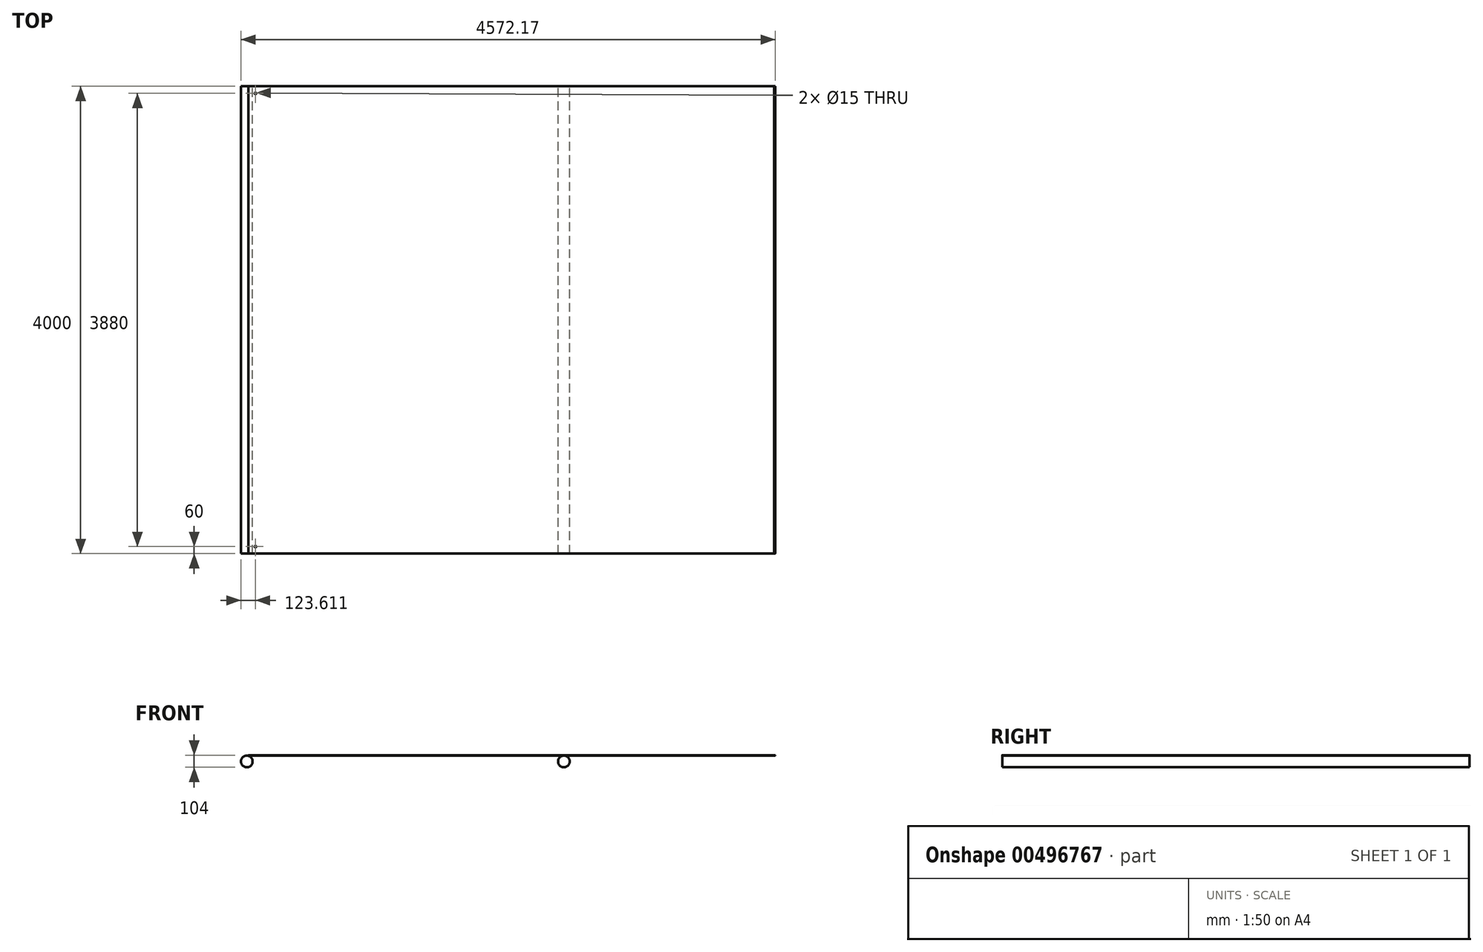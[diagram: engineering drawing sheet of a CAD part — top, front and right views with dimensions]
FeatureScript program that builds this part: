
annotation { "Feature Type Name" : "Feature", "Feature Type Description" : "" }
export const myFeature = defineFeature(function(context is Context, id is Id, definition is map)
    precondition{}
    {
        {
            var Q0;
            Q0=qCreatedBy(makeId("Front.planeOp"),FACE);
            var sketch = newSketch(context, id + "F0", { "sketchPlane" : qUnion([Q0])});
            skLineSegment(sketch, "E0", {"start": v(-1765.1, -2.59) * mm, "end": v(2734.9, -2.59) * mm});
            skCircle(sketch, "E1", {"center": v(934.9, -52.59) * mm, "radius": 50 * mm});
            skCircle(sketch, "E2", {"center": v(-1778.7, -52.59) * mm, "radius": 50 * mm});
            skLineSegment(sketch, "E3", {"start": v(-1765.1, -2.59) * mm, "end": v(-1765.1, 0.41) * mm});
            skLineSegment(sketch, "E4", {"start": v(-1765.1, 0.41) * mm, "end": v(2734.9, 0.41) * mm});
            skLineSegment(sketch, "E5", {"start": v(2734.9, -2.59) * mm, "end": v(2734.9, 0.41) * mm});
            skCircle(sketch, "E6", {"center": v(2740.96, -1.09) * mm, "radius": 2.5 * mm});
            skPoint(sketch, "E6.centerSnap0", {"position": v(2734.9, -1.09) * mm});
            skLineSegment(sketch, "E7", {"start": v(2734.9, -0.46) * mm, "end": v(2738.54, -0.46) * mm});
            skLineSegment(sketch, "E8", {"start": v(2734.9, -1.53) * mm, "end": v(2738.5, -1.53) * mm});
            skSolve(sketch);
        }
        {
            var Q0;
            Q0 = qSketchRegion(id + "F0", true);
            extrude(context, id + "F1", {"entities" : qUnion([Q0]), "depth" : 4000 * mm, "offsetDistance" : 25 * mm});
        }
        {
            var Q0;
            Q0=makeQuery(id+"F1.opExtrude","SWEPT_FACE",FACE,{"disambiguationData":[OSD([sQuery(id+"F0.wireOp",EDGE,"E4")])]});
            var sketch = newSketch(context, id + "F2", { "sketchPlane" : qUnion([Q0])});
            skPoint(sketch, "E9", {"position": v(-1705.1, -60) * mm});
            skSolve(sketch);
        }
        {
            var Q0;
            Q0=sQuery(id+"F2.wireOp",VERTEX,"E9");
            var Q1;
            Q1=makeQuery(id+"F1.opExtrude","SWEPT_BODY",BODY,{"disambiguationData":[OSD([sQuery(id+"F0.wireOp",EDGE,"E0"),sQuery(id+"F0.wireOp",EDGE,"E3"),sQuery(id+"F0.wireOp",EDGE,"E4"),sQuery(id+"F0.wireOp",EDGE,"E5"),sQuery(id+"F0.wireOp",EDGE,"E6"),sQuery(id+"F0.wireOp",EDGE,"E7"),sQuery(id+"F0.wireOp",EDGE,"E8")])]});
            hole(context, id + "F3", {"style" : HoleStyle.SIMPLE, "endStyle" : HoleEndStyle.THROUGH, "holeDiameter" : 15 * mm, "majorDiameter" : 5 * mm, "isTappedThrough" : true, "tappedDepth" : 12 * mm, "tapClearance" : 3, "locations" : qUnion([Q0]), "scope" : qUnion([Q1])});
        }
        {
            var Q0;
            {var subQ0=sQuery(id+"F0.wireOp",EDGE,"E4");Q0=makeQuery(id+"F2.imprint","IMPRINT",FACE,{"disambiguationData":[TD([[makeQuery(id+"F2.imprint","IMPRINT",EDGE,{"derivedFrom":makeQuery(id+"F1.opExtrude","CAP_EDGE",EDGE,{"disambiguationData":[OSD([subQ0])],"isStart":true})}),-1.0]])]});}
            var sketch = newSketch(context, id + "F4", { "sketchPlane" : qUnion([Q0])});
            skPoint(sketch, "E10", {"position": v(-1705.1, -3940) * mm});
            skSolve(sketch);
        }
        {
            var Q0;
            Q0=sQuery(id+"F4.wireOp",VERTEX,"E10");
            var Q1;
            Q1=makeQuery(id+"F1.opExtrude","SWEPT_BODY",BODY,{"disambiguationData":[OSD([sQuery(id+"F0.wireOp",EDGE,"E0"),sQuery(id+"F0.wireOp",EDGE,"E3"),sQuery(id+"F0.wireOp",EDGE,"E4"),sQuery(id+"F0.wireOp",EDGE,"E5"),sQuery(id+"F0.wireOp",EDGE,"E6"),sQuery(id+"F0.wireOp",EDGE,"E7"),sQuery(id+"F0.wireOp",EDGE,"E8")])]});
            hole(context, id + "F5", {"style" : HoleStyle.SIMPLE, "endStyle" : HoleEndStyle.THROUGH, "holeDiameter" : 15 * mm, "majorDiameter" : 5 * mm, "isTappedThrough" : true, "tappedDepth" : 12 * mm, "tapClearance" : 3, "locations" : qUnion([Q0]), "scope" : qUnion([Q1])});
        }
    });
